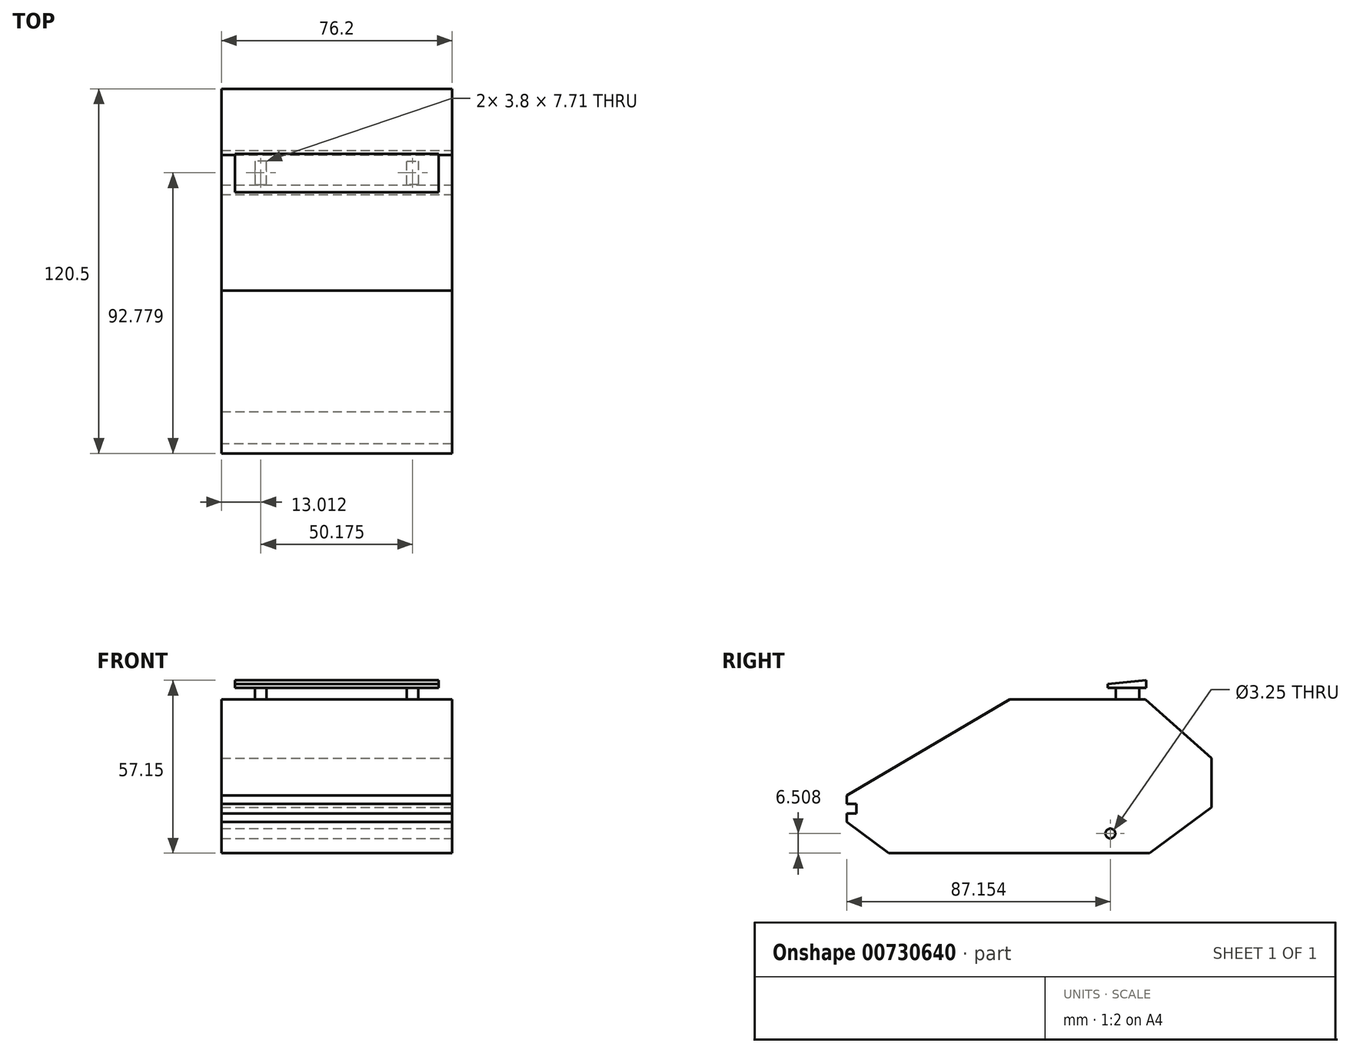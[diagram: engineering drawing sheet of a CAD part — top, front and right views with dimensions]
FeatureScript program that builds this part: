
annotation { "Feature Type Name" : "Feature", "Feature Type Description" : "" }
export const myFeature = defineFeature(function(context is Context, id is Id, definition is map)
    precondition{}
    {
        {
            var Q0;
            Q0=qCreatedBy(makeId("Top.planeOp"),FACE);
            var sketch = newSketch(context, id + "F0", { "sketchPlane" : qUnion([Q0])});
            skLineSegment(sketch, "E0.bottom", {"start": v(-38.1, 63.5) * mm, "end": v(38.1, 63.5) * mm});
            skLineSegment(sketch, "E0.top", {"start": v(-38.1, -63.5) * mm, "end": v(38.1, -63.5) * mm});
            skLineSegment(sketch, "E0.left", {"start": v(-38.1, 63.5) * mm, "end": v(-38.1, -63.5) * mm});
            skLineSegment(sketch, "E0.right", {"start": v(38.1, 63.5) * mm, "end": v(38.1, -63.5) * mm});
            skPoint(sketch, "E0.middle", {"position": v(0, 0) * mm});
            skSolve(sketch);
        }
        {
            var Q0;
            Q0=makeQuery(id+"F0.imprint","IMPRINT",FACE,{"disambiguationData":[TD([[makeQuery(id+"F0.imprint","IMPRINT",EDGE,{"derivedFrom":sQuery(id+"F0.wireOp",EDGE,"E0.bottom")}),-1.0]])]});
            extrude(context, id + "F1", {"entities" : qUnion([Q0]), "depth" : 25.4 * mm, "offsetDistance" : 25.4 * mm});
        }
        {
            var Q0;
            Q0=makeQuery(id+"F1.opExtrude","CAP_FACE",FACE,{"disambiguationData":[OSD([sQuery(id+"F0.wireOp",EDGE,"E0.bottom"),sQuery(id+"F0.wireOp",EDGE,"E0.top"),sQuery(id+"F0.wireOp",EDGE,"E0.left"),sQuery(id+"F0.wireOp",EDGE,"E0.right")])],"isStart":false});
            var sketch = newSketch(context, id + "F2", { "sketchPlane" : qUnion([Q0])});
            skLineSegment(sketch, "E1", {"start": v(-38.1, -3.11) * mm, "end": v(38.1, -3.11) * mm});
            skSolve(sketch);
        }
        {
            var Q0;
            Q0 = qSketchRegion(id + "F2", true);
            var Q1;
            {var subQ0=sQuery(id+"F2.wireOp",EDGE,"E1");Q1=makeQuery(id+"F2.imprint","IMPRINT",FACE,{"disambiguationData":[TD([[makeQuery(id+"F2.imprint","IMPRINT",EDGE,{"derivedFrom":subQ0}),-1.0]])]});}
            extrude(context, id + "F3", {"entities" : qUnion([Q0, Q1]), "operationType" : NewBodyOperationType.ADD, "depth" : 25.4 * mm, "offsetDistance" : 25.4 * mm});
        }
        {
            var Q0;
            {var subQ0=sQuery(id+"F0.wireOp",EDGE,"E0.right");Q0=makeQuery(id+"F3.boolean.opBoolean","MERGE",FACE,{"derivedFrom":[makeQuery(id+"F1.opExtrude","SWEPT_FACE",FACE,{"disambiguationData":[OSD([subQ0])]}),makeQuery(id+"F3.opExtrude","SWEPT_FACE",FACE,{"disambiguationData":[OSD([subQ0])]})]});}
            var sketch = newSketch(context, id + "F4", { "sketchPlane" : qUnion([Q0])});
            skLineSegment(sketch, "E2", {"start": v(-3.11, 50.8) * mm, "end": v(-63.5, 15.2) * mm});
            skSolve(sketch);
        }
        {
            var Q0;
            Q0=makeQuery(id+"F1.opExtrude","CAP_FACE",FACE,{"disambiguationData":[OSD([sQuery(id+"F0.wireOp",EDGE,"E0.bottom"),sQuery(id+"F0.wireOp",EDGE,"E0.top"),sQuery(id+"F0.wireOp",EDGE,"E0.left"),sQuery(id+"F0.wireOp",EDGE,"E0.right")])],"isStart":false});
            extrude(context, id + "F5", {"entities" : qUnion([Q0]), "operationType" : NewBodyOperationType.ADD, "depth" : 25.4 * mm, "offsetDistance" : 25.4 * mm});
        }
        {
            var Q0;
            {var subQ0=sQuery(id+"F0.wireOp",EDGE,"E0.right");Q0=makeQuery(id+"F5.boolean.opBoolean","MERGE",FACE,{"derivedFrom":[makeQuery(id+"F3.boolean.opBoolean","MERGE",FACE,{"derivedFrom":[makeQuery(id+"F1.opExtrude","SWEPT_FACE",FACE,{"disambiguationData":[OSD([subQ0])]}),makeQuery(id+"F3.opExtrude","SWEPT_FACE",FACE,{"disambiguationData":[OSD([subQ0])]})]}),makeQuery(id+"F5.opExtrude","SWEPT_FACE",FACE,{"disambiguationData":[OSD([subQ0])]})]});}
            var sketch = newSketch(context, id + "F6", { "sketchPlane" : qUnion([Q0])});
            skLineSegment(sketch, "E3", {"start": v(41.7, 50.8) * mm, "end": v(63.5, 31.47) * mm});
            skSolve(sketch);
        }
        {
            var Q0;
            {var subQ0=sQuery(id+"F0.wireOp",EDGE,"E0.right");var subQ1=sQuery(id+"F0.wireOp",EDGE,"E0.left");var subQ2=sQuery(id+"F0.wireOp",EDGE,"E0.top");Q0=makeQuery(id+"F5.boolean.opBoolean","MERGE",FACE,{"derivedFrom":[makeQuery(id+"F3.opExtrude","CAP_FACE",FACE,{"disambiguationData":[OSD([subQ2,subQ1,subQ0,sQuery(id+"F2.wireOp",EDGE,"E1")])],"isStart":false}),makeQuery(id+"F5.opExtrude","CAP_FACE",FACE,{"disambiguationData":[OSD([sQuery(id+"F0.wireOp",EDGE,"E0.bottom"),subQ2,subQ1,subQ0])],"isStart":false})]});}
            var sketch = newSketch(context, id + "F7", { "sketchPlane" : qUnion([Q0])});
            skLineSegment(sketch, "E4", {"start": v(26.99, 39.64) * mm, "end": v(26.99, 31.92) * mm});
            skLineSegment(sketch, "E5", {"start": v(26.99, 31.92) * mm, "end": v(23.19, 31.92) * mm});
            skLineSegment(sketch, "E6", {"start": v(23.19, 31.92) * mm, "end": v(23.19, 39.64) * mm});
            skLineSegment(sketch, "E7", {"start": v(23.19, 39.64) * mm, "end": v(26.99, 39.64) * mm});
            skLineSegment(sketch, "E8.MirrorCS", {"start": v(-23.19, 39.64) * mm, "end": v(-26.99, 39.64) * mm});
            skLineSegment(sketch, "E9.MirrorCS", {"start": v(-23.19, 31.92) * mm, "end": v(-23.19, 39.64) * mm});
            skLineSegment(sketch, "E10.MirrorCS", {"start": v(-26.99, 39.64) * mm, "end": v(-26.99, 31.92) * mm});
            skLineSegment(sketch, "E11.MirrorCS", {"start": v(-26.99, 31.92) * mm, "end": v(-23.19, 31.92) * mm});
            skSolve(sketch);
        }
        {
            var Q0;
            Q0 = qSketchRegion(id + "F7", true);
            extrude(context, id + "F8", {"entities" : qUnion([Q0]), "operationType" : NewBodyOperationType.ADD, "depth" : 3.8 * mm, "offsetDistance" : 25.4 * mm});
        }
        {
            var Q0;
            Q0=makeQuery(id+"F8.opExtrude","CAP_FACE",FACE,{"disambiguationData":[OSD([sQuery(id+"F7.wireOp",EDGE,"E4"),sQuery(id+"F7.wireOp",EDGE,"E5"),sQuery(id+"F7.wireOp",EDGE,"E6"),sQuery(id+"F7.wireOp",EDGE,"E7")])],"isStart":false});
            var sketch = newSketch(context, id + "F9", { "sketchPlane" : qUnion([Q0])});
            skLineSegment(sketch, "E12", {"start": v(33.7, 42) * mm, "end": v(33.7, 29.3) * mm});
            skLineSegment(sketch, "E13.MirrorCS", {"start": v(-33.7, 42) * mm, "end": v(-33.7, 29.3) * mm});
            skLineSegment(sketch, "E14", {"start": v(-33.7, 42) * mm, "end": v(33.7, 42) * mm});
            skLineSegment(sketch, "E15", {"start": v(33.7, 29.3) * mm, "end": v(-33.7, 29.3) * mm});
            skSolve(sketch);
        }
        {
            var Q0;
            Q0 = qSketchRegion(id + "F9", true);
            extrude(context, id + "F10", {"entities" : qUnion([Q0]), "operationType" : NewBodyOperationType.ADD, "depth" : 2.54 * mm, "offsetDistance" : 25.4 * mm});
        }
        {
            var Q0;
            {var subQ0=sQuery(id+"F4.wireOp",EDGE,"E2");Q0=makeQuery(id+"F4.imprint","IMPRINT",FACE,{"disambiguationData":[TD([[makeQuery(id+"F4.imprint","IMPRINT",EDGE,{"derivedFrom":subQ0}),-1.0]])]});}
            extrude(context, id + "F11", {"entities" : qUnion([Q0]), "operationType" : NewBodyOperationType.ADD, "depth" : 25.4 * mm, "offsetDistance" : 25.4 * mm});
        }
        {
            var Q0;
            Q0=makeQuery(id+"F11.opExtrude","CAP_FACE",FACE,{"disambiguationData":[OSD([sQuery(id+"F0.wireOp",EDGE,"E0.top"),sQuery(id+"F0.wireOp",EDGE,"E0.right"),sQuery(id+"F4.wireOp",EDGE,"E2")])],"isStart":false});
            var sketch = newSketch(context, id + "F12", { "sketchPlane" : qUnion([Q0])});
            skSolve(sketch);
        }
        {
            var Q0;
            Q0 = qSketchRegion(id + "F12", true);
            var Q1;
            Q1=makeQuery(id+"F12.imprint","IMPRINT",FACE,{"disambiguationData":[TD([[makeQuery(id+"F12.imprint","IMPRINT",EDGE,{"derivedFrom":makeQuery(id+"F11.opExtrude","CAP_EDGE",EDGE,{"disambiguationData":[OSD([sQuery(id+"F4.wireOp",EDGE,"E2")])],"isStart":false})}),-1.0]])]});
            extrude(context, id + "F13", {"entities" : qUnion([Q0, Q1]), "operationType" : NewBodyOperationType.REMOVE, "oppositeDirection" : true, "depth" : 119.38 * mm, "offsetDistance" : 25.4 * mm});
        }
        {
            var Q0;
            {var subQ0=sQuery(id+"F6.wireOp",EDGE,"E3");Q0=makeQuery(id+"F6.imprint","IMPRINT",FACE,{"disambiguationData":[TD([[makeQuery(id+"F6.imprint","IMPRINT",EDGE,{"derivedFrom":subQ0}),1.0]])]});}
            extrude(context, id + "F14", {"entities" : qUnion([Q0]), "operationType" : NewBodyOperationType.REMOVE, "oppositeDirection" : true, "depth" : 158 * mm, "offsetDistance" : 25.4 * mm});
        }
        {
            var Q0;
            Q0=makeQuery(id+"F10.opExtrude","SWEPT_FACE",FACE,{"disambiguationData":[OSD([sQuery(id+"F9.wireOp",EDGE,"E12")])]});
            var sketch = newSketch(context, id + "F15", { "sketchPlane" : qUnion([Q0])});
            skLineSegment(sketch, "E16", {"start": v(29.3, 55.88) * mm, "end": v(42, 57.15) * mm});
            skSolve(sketch);
        }
        {
            var Q0;
            {var subQ0=sQuery(id+"F15.wireOp",EDGE,"E16");Q0=makeQuery(id+"F15.imprint","IMPRINT",FACE,{"disambiguationData":[TD([[makeQuery(id+"F15.imprint","IMPRINT",EDGE,{"derivedFrom":subQ0}),1.0]])]});}
            extrude(context, id + "F16", {"entities" : qUnion([Q0]), "operationType" : NewBodyOperationType.REMOVE, "oppositeDirection" : true, "depth" : 160.73 * mm, "offsetDistance" : 25.4 * mm});
        }
        {
            var Q0;
            {var subQ0=sQuery(id+"F0.wireOp",EDGE,"E0.right");Q0=makeQuery(id+"F5.boolean.opBoolean","MERGE",FACE,{"derivedFrom":[makeQuery(id+"F3.boolean.opBoolean","MERGE",FACE,{"derivedFrom":[makeQuery(id+"F1.opExtrude","SWEPT_FACE",FACE,{"disambiguationData":[OSD([subQ0])]}),makeQuery(id+"F3.opExtrude","SWEPT_FACE",FACE,{"disambiguationData":[OSD([subQ0])]})]}),makeQuery(id+"F5.opExtrude","SWEPT_FACE",FACE,{"disambiguationData":[OSD([subQ0])]})]});}
            var sketch = newSketch(context, id + "F17", { "sketchPlane" : qUnion([Q0])});
            skLineSegment(sketch, "E17", {"start": v(-63.5, 15.2) * mm, "end": v(63.5, 15.2) * mm});
            skLineSegment(sketch, "E18", {"start": v(-63.5, 15.2) * mm, "end": v(-43.16, 0) * mm});
            skLineSegment(sketch, "E19", {"start": v(63.5, 15.2) * mm, "end": v(43.16, 0) * mm});
            skSolve(sketch);
        }
        {
            var Q0;
            {var subQ0=sQuery(id+"F17.wireOp",EDGE,"E18");Q0=makeQuery(id+"F17.imprint","IMPRINT",FACE,{"disambiguationData":[TD([[makeQuery(id+"F17.imprint","IMPRINT",EDGE,{"derivedFrom":subQ0}),-1.0]])]});}
            extrude(context, id + "F18", {"entities" : qUnion([Q0]), "operationType" : NewBodyOperationType.REMOVE, "oppositeDirection" : true, "depth" : 107.44 * mm, "offsetDistance" : 25.4 * mm});
        }
        {
            var Q0;
            {var subQ0=sQuery(id+"F17.wireOp",EDGE,"E19");Q0=makeQuery(id+"F17.imprint","IMPRINT",FACE,{"disambiguationData":[TD([[makeQuery(id+"F17.imprint","IMPRINT",EDGE,{"derivedFrom":subQ0}),1.0]])]});}
            extrude(context, id + "F19", {"entities" : qUnion([Q0]), "operationType" : NewBodyOperationType.REMOVE, "oppositeDirection" : true, "depth" : 146.05 * mm, "offsetDistance" : 25.4 * mm});
        }
        {
            var Q0;
            {var subQ0=sQuery(id+"F0.wireOp",EDGE,"E0.left");Q0=makeQuery(id+"F5.boolean.opBoolean","MERGE",FACE,{"derivedFrom":[makeQuery(id+"F3.boolean.opBoolean","MERGE",FACE,{"derivedFrom":[makeQuery(id+"F1.opExtrude","SWEPT_FACE",FACE,{"disambiguationData":[OSD([subQ0])]}),makeQuery(id+"F3.opExtrude","SWEPT_FACE",FACE,{"disambiguationData":[OSD([subQ0])]})]}),makeQuery(id+"F5.opExtrude","SWEPT_FACE",FACE,{"disambiguationData":[OSD([subQ0])]})]});}
            var sketch = newSketch(context, id + "F20", { "sketchPlane" : qUnion([Q0])});
            skSolve(sketch);
        }
        {
            var Q0;
            {var subQ0=sQuery(id+"F0.wireOp",EDGE,"E0.left");Q0=makeQuery(id+"F20.imprint","IMPRINT",FACE,{"disambiguationData":[TD([[makeQuery(id+"F20.imprint","IMPRINT",EDGE,{"derivedFrom":makeQuery(id+"F1.opExtrude","CAP_EDGE",EDGE,{"disambiguationData":[OSD([subQ0])],"isStart":true})}),1.0]])]});}
            var sketch = newSketch(context, id + "F21", { "sketchPlane" : qUnion([Q0])});
            skLineSegment(sketch, "E20", {"start": v(57, 24.4) * mm, "end": v(57, 6.13) * mm});
            skLineSegment(sketch, "E21", {"start": v(57, 24.4) * mm, "end": v(67.44, 13.23) * mm});
            skLineSegment(sketch, "E22", {"start": v(67.44, 13.23) * mm, "end": v(57, 6.13) * mm});
            skSolve(sketch);
        }
        {
            var Q0;
            Q0 = qSketchRegion(id + "F21", true);
            extrude(context, id + "F22", {"entities" : qUnion([Q0]), "operationType" : NewBodyOperationType.REMOVE, "oppositeDirection" : true, "depth" : 175.5 * mm, "offsetDistance" : 25.4 * mm});
        }
        {
            var Q0;
            {var subQ0=sQuery(id+"F0.wireOp",EDGE,"E0.right");Q0=makeQuery(id+"F5.boolean.opBoolean","MERGE",FACE,{"derivedFrom":[makeQuery(id+"F3.boolean.opBoolean","MERGE",FACE,{"derivedFrom":[makeQuery(id+"F1.opExtrude","SWEPT_FACE",FACE,{"disambiguationData":[OSD([subQ0])]}),makeQuery(id+"F3.opExtrude","SWEPT_FACE",FACE,{"disambiguationData":[OSD([subQ0])]})]}),makeQuery(id+"F5.opExtrude","SWEPT_FACE",FACE,{"disambiguationData":[OSD([subQ0])]})]});}
            var sketch = newSketch(context, id + "F23", { "sketchPlane" : qUnion([Q0])});
            skCircle(sketch, "E23", {"center": v(30.15, 6.5) * mm, "radius": 1.63 * mm});
            skSolve(sketch);
        }
        {
            var Q0;
            Q0 = qSketchRegion(id + "F23", true);
            extrude(context, id + "F24", {"entities" : qUnion([Q0]), "operationType" : NewBodyOperationType.REMOVE, "oppositeDirection" : true, "depth" : 94.74 * mm, "offsetDistance" : 25.4 * mm});
        }
        {
            var Q0;
            Q0=makeQuery(id+"F22.boolean.opBoolean","COPY",FACE,{"derivedFrom":makeQuery(id+"F22.opExtrude","SWEPT_FACE",FACE,{"disambiguationData":[OSD([sQuery(id+"F21.wireOp",EDGE,"E20")])]})});
            var sketch = newSketch(context, id + "F25", { "sketchPlane" : qUnion([Q0])});
            skLineSegment(sketch, "E24.bottom", {"start": v(42.95, 13.14) * mm, "end": v(-42.95, 13.14) * mm});
            skLineSegment(sketch, "E24.top", {"start": v(42.95, 16.32) * mm, "end": v(-42.95, 16.32) * mm});
            skLineSegment(sketch, "E24.left", {"start": v(42.95, 13.14) * mm, "end": v(42.95, 16.32) * mm});
            skLineSegment(sketch, "E24.right", {"start": v(-42.95, 13.14) * mm, "end": v(-42.95, 16.32) * mm});
            skPoint(sketch, "E24.middle", {"position": v(0, 14.73) * mm});
            skSolve(sketch);
        }
        {
            var Q0;
            Q0 = qSketchRegion(id + "F25", true);
            extrude(context, id + "F26", {"entities" : qUnion([Q0]), "operationType" : NewBodyOperationType.REMOVE, "oppositeDirection" : true, "depth" : 3.17 * mm, "offsetDistance" : 25.4 * mm});
        }
    });
